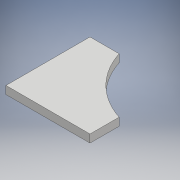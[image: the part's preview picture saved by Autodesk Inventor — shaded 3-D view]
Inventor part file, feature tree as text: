
AUTODESK INVENTOR PART (.ipt)
format: ipt  version: 2018 (Build 220112000, 112)  size: 102,912 bytes
history: native  units: mm
features: other x1, extrude x1, sketch x1
ambient origin geometry x8: Origin, YZ Plane, XZ Plane, XY Plane, X Axis, Y Axis, Z Axis, Center Point
bodies: Body1 (feature_tree)
feature tree (3):
  other  "Bryła1"
  extrude  "Wyciągnięcie proste1"  Depth=6.0mm TaperAngle=0.0deg
  sketch  "Szkic1"
